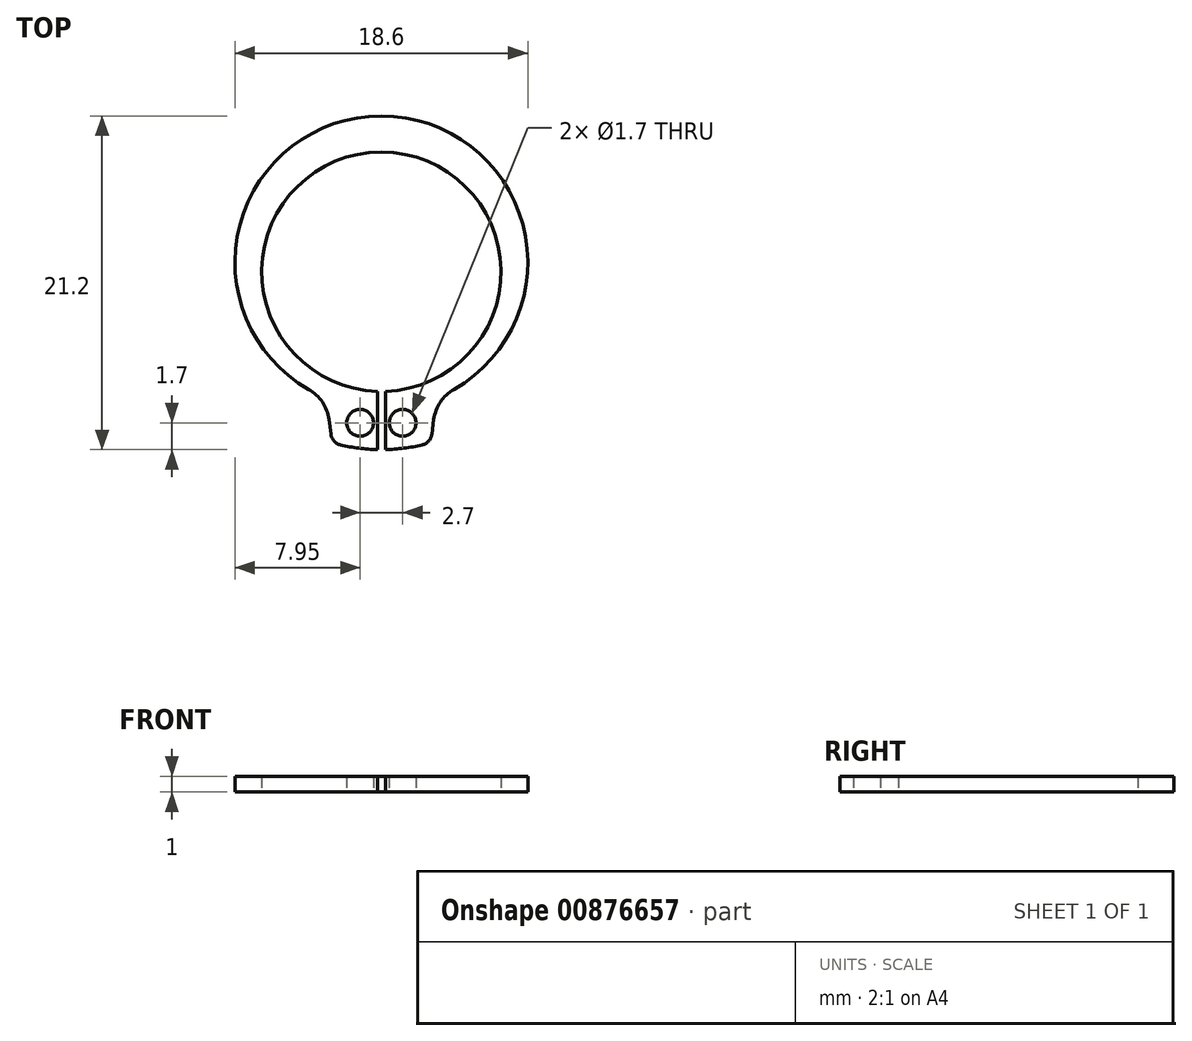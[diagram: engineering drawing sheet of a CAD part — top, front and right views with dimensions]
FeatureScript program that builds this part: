
annotation { "Feature Type Name" : "Feature", "Feature Type Description" : "" }
export const myFeature = defineFeature(function(context is Context, id is Id, definition is map)
    precondition{}
    {
        {
            var Q0;
            Q0=qCreatedBy(makeId("Top.planeOp"),FACE);
            var sketch = newSketch(context, id + "F0", { "sketchPlane" : qUnion([Q0])});
            skArc(sketch, "E0", {"start": v(0.25, -7.6) * mm, "mid": v(0, 7.6) * mm, "end": v(-0.25, -7.6) * mm});
            skArc(sketch, "E1", {"start": v(4.62, -7.47) * mm, "mid": v(0, 9.9) * mm, "end": v(-4.62, -7.47) * mm});
            skLineSegment(sketch, "E2", {"start": v(0, 0) * mm, "end": v(0, -9.6) * mm, "construction": true});
            skCircle(sketch, "E3", {"center": v(1.35, -9.6) * mm, "radius": 0.85 * mm});
            skCircle(sketch, "E4.MirrorC", {"center": v(-1.35, -9.6) * mm, "radius": 0.85 * mm});
            skLineSegment(sketch, "E5", {"start": v(0.25, -11.3) * mm, "end": v(0.25, -7.6) * mm});
            skLineSegment(sketch, "E6.MirrorCS", {"start": v(-0.25, -11.3) * mm, "end": v(-0.25, -7.6) * mm});
            skLineSegment(sketch, "E7", {"start": v(3.2, -10.32) * mm, "end": v(3.33, -9.4) * mm});
            skLineSegment(sketch, "E8.MirrorCS", {"start": v(-3.2, -10.32) * mm, "end": v(-3.33, -9.4) * mm});
            skArc(sketch, "E9", {"start": v(-2.6, -11) * mm, "mid": v(-1.43, -11.2) * mm, "end": v(-0.25, -11.3) * mm});
            skArc(sketch, "E10.trimOffspring", {"start": v(0.25, -11.3) * mm, "mid": v(1.43, -11.2) * mm, "end": v(2.6, -11) * mm});
            skPoint(sketch, "E11.visualSharp", {"position": v(3.51, -8.01) * mm});
            skArc(sketch, "E11.filletArc", {"start": v(4.62, -7.47) * mm, "mid": v(3.75, -8.28) * mm, "end": v(3.33, -9.4) * mm});
            skPoint(sketch, "E12.visualSharp", {"position": v(-3.51, -8.01) * mm});
            skArc(sketch, "E12.filletArc", {"start": v(-3.33, -9.4) * mm, "mid": v(-3.75, -8.28) * mm, "end": v(-4.62, -7.47) * mm});
            skPoint(sketch, "E13.visualSharp", {"position": v(3.14, -10.86) * mm});
            skArc(sketch, "E13.filletArc", {"start": v(2.6, -11) * mm, "mid": v(3, -10.76) * mm, "end": v(3.2, -10.32) * mm});
            skPoint(sketch, "E14.visualSharp", {"position": v(-3.14, -10.86) * mm});
            skArc(sketch, "E14.filletArc", {"start": v(-3.2, -10.32) * mm, "mid": v(-3, -10.76) * mm, "end": v(-2.6, -11) * mm});
            skLineSegment(sketch, "E15", {"start": v(0, 0) * mm, "end": v(4.62, -7.47) * mm, "construction": true});
            skLineSegment(sketch, "E16", {"start": v(0, 0) * mm, "end": v(-4.62, -7.47) * mm, "construction": true});
            skSolve(sketch);
        }
        {
            var Q0;
            Q0 = qSketchRegion(id + "F0", true);
            extrude(context, id + "F1", {"entities" : qUnion([Q0]), "depth" : 1 * mm, "offsetDistance" : 25 * mm});
        }
    });
